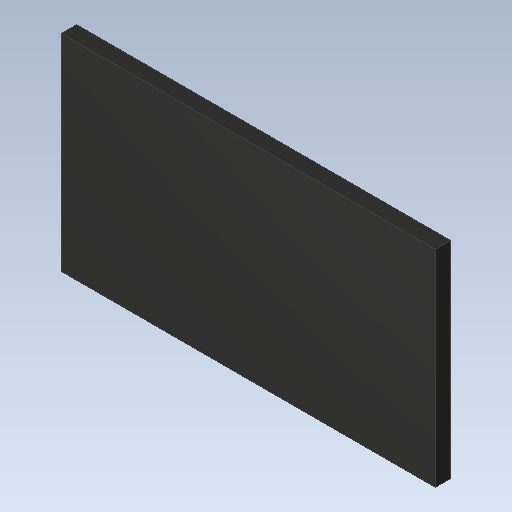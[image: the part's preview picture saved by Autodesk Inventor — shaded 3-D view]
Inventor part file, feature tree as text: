
AUTODESK INVENTOR PART (.ipt)
format: ipt  version: 2020 (Build 240168000, 168)  size: 86,528 bytes
history: imported  units: in
note: dims shown in document units (in); Inventor stores cm internally (conversion verified against a paired STEP export)
features: imported_body x1
ambient origin geometry x8: Origin, YZ Plane, XZ Plane, XY Plane, X Axis, Y Axis, Z Axis, Center Point
bodies: Solid1 (imported_parasolid), Body1 (imported_parasolid)
feature tree (1):
  imported_body  NMx_Import_Brep_tag  [imported B-rep: ~6 faces, bbox_mm=[2.4508, 1.3508, 0.1]]
